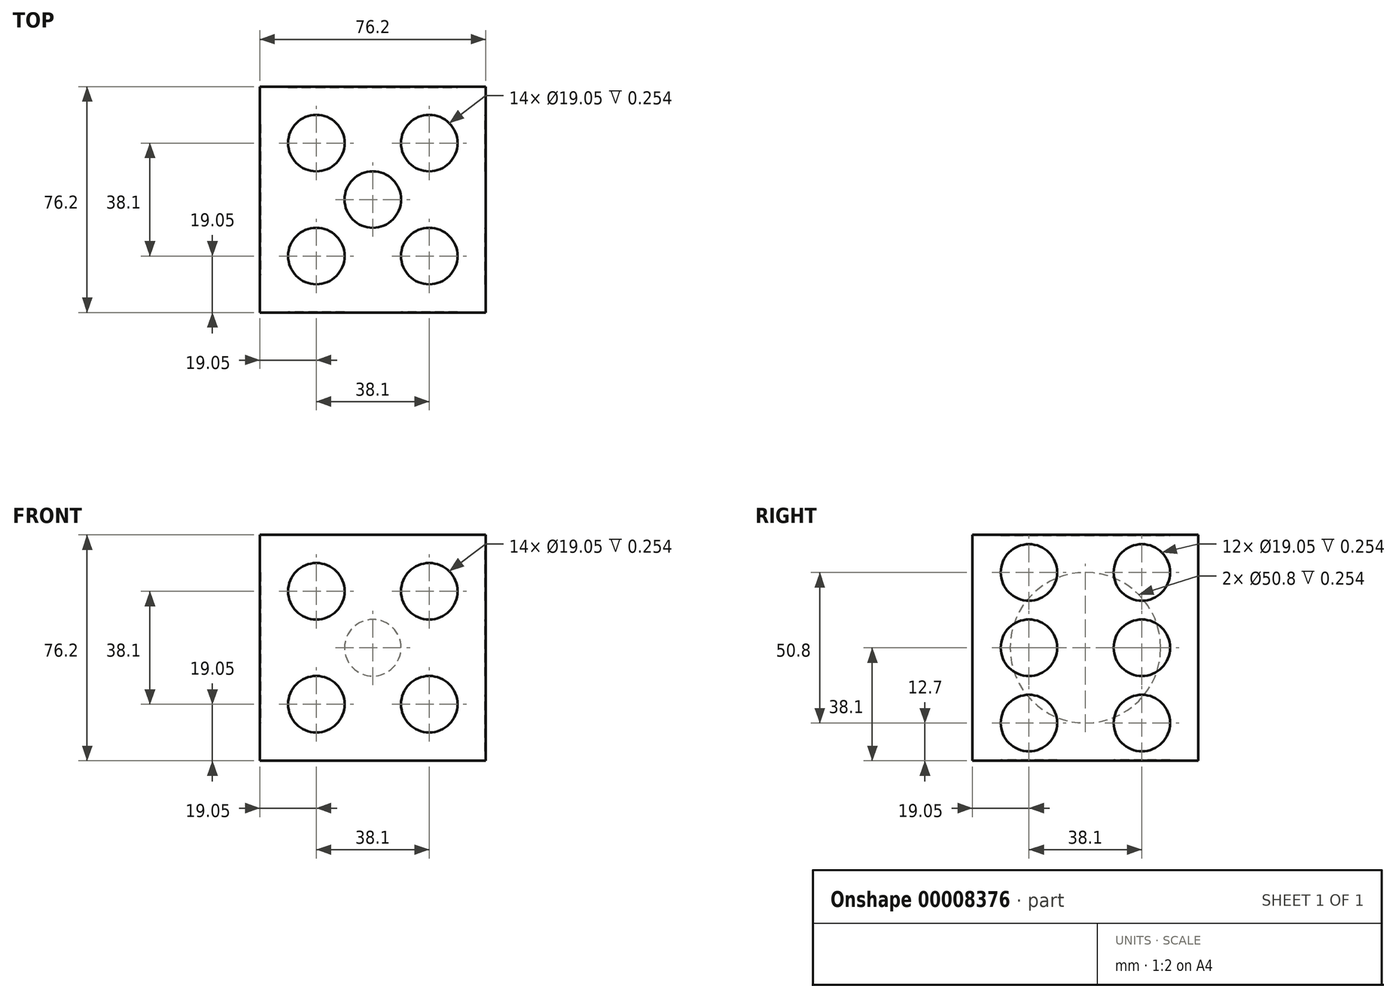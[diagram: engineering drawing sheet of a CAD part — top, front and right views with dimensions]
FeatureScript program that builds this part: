
annotation { "Feature Type Name" : "Feature", "Feature Type Description" : "" }
export const myFeature = defineFeature(function(context is Context, id is Id, definition is map)
    precondition{}
    {
        {
            var Q0;
            Q0=qCreatedBy(makeId("Top.planeOp"),FACE);
            var sketch = newSketch(context, id + "F0", { "sketchPlane" : qUnion([Q0])});
            skLineSegment(sketch, "E0.rect.bottom", {"start": v(38.1, -38.1) * mm, "end": v(-38.1, -38.1) * mm});
            skLineSegment(sketch, "E0.rect.top", {"start": v(38.1, 38.1) * mm, "end": v(-38.1, 38.1) * mm});
            skLineSegment(sketch, "E0.rect.left", {"start": v(38.1, -38.1) * mm, "end": v(38.1, 38.1) * mm});
            skLineSegment(sketch, "E0.rect.right", {"start": v(-38.1, -38.1) * mm, "end": v(-38.1, 38.1) * mm});
            skPoint(sketch, "E0.rect.middle", {"position": v(0, 0) * mm});
            skSolve(sketch);
        }
        {
            var Q0;
            Q0=makeQuery(id+"F0.imprint","IMPRINT",FACE,{"disambiguationData":[TD([[makeQuery(id+"F0.imprint","IMPRINT",EDGE,{"derivedFrom":sQuery(id+"F0.wireOp",EDGE,"E0.rect.bottom")}),-1.0]])]});
            extrude(context, id + "F1", {"entities" : qUnion([Q0]), "depth" : 38.1 * mm, "hasSecondDirection" : true, "secondDirectionOppositeDirection" : true, "secondDirectionDepth" : 38.1 * mm});
        }
        {
            var Q0;
            Q0=makeQuery(id+"F1.opExtrude","SWEPT_FACE",FACE,{"disambiguationData":[OSD([sQuery(id+"F0.wireOp",EDGE,"E0.rect.right")])]});
            var sketch = newSketch(context, id + "F2", { "sketchPlane" : qUnion([Q0])});
            skCircle(sketch, "E1", {"center": v(0, 0) * mm, "radius": 25.4 * mm});
            skSolve(sketch);
        }
        {
            var Q0;
            Q0=makeQuery(id+"F2.imprint","IMPRINT",FACE,{"disambiguationData":[TD([[makeQuery(id+"F2.imprint","IMPRINT",EDGE,{"derivedFrom":sQuery(id+"F2.wireOp",EDGE,"E1")}),1.0]])]});
            extrude(context, id + "F3", {"entities" : qUnion([Q0]), "operationType" : NewBodyOperationType.REMOVE, "oppositeDirection" : true, "depth" : 0.25 * mm});
        }
        {
            var Q0;
            Q0=makeQuery(id+"F1.opExtrude","SWEPT_FACE",FACE,{"disambiguationData":[OSD([sQuery(id+"F0.wireOp",EDGE,"E0.rect.left")])]});
            var sketch = newSketch(context, id + "F4", { "sketchPlane" : qUnion([Q0])});
            skCircle(sketch, "E2", {"center": v(-19.05, 25.4) * mm, "radius": 9.53 * mm});
            skCircle(sketch, "E3", {"center": v(-19.05, 0) * mm, "radius": 9.53 * mm});
            skCircle(sketch, "E4", {"center": v(-19.05, -25.4) * mm, "radius": 9.53 * mm});
            skCircle(sketch, "E5", {"center": v(19.05, -25.4) * mm, "radius": 9.53 * mm});
            skCircle(sketch, "E6", {"center": v(19.05, 0) * mm, "radius": 9.53 * mm});
            skCircle(sketch, "E7", {"center": v(19.05, 25.4) * mm, "radius": 9.53 * mm});
            skSolve(sketch);
        }
        {
            var Q0;
            Q0=makeQuery(id+"F4.imprint","IMPRINT",FACE,{"disambiguationData":[TD([[makeQuery(id+"F4.imprint","IMPRINT",EDGE,{"derivedFrom":sQuery(id+"F4.wireOp",EDGE,"E2")}),1.0]])]});
            var Q1;
            Q1=makeQuery(id+"F4.imprint","IMPRINT",FACE,{"disambiguationData":[TD([[makeQuery(id+"F4.imprint","IMPRINT",EDGE,{"derivedFrom":sQuery(id+"F4.wireOp",EDGE,"E7")}),1.0]])]});
            var Q2;
            Q2=makeQuery(id+"F4.imprint","IMPRINT",FACE,{"disambiguationData":[TD([[makeQuery(id+"F4.imprint","IMPRINT",EDGE,{"derivedFrom":sQuery(id+"F4.wireOp",EDGE,"E6")}),1.0]])]});
            var Q3;
            Q3=makeQuery(id+"F4.imprint","IMPRINT",FACE,{"disambiguationData":[TD([[makeQuery(id+"F4.imprint","IMPRINT",EDGE,{"derivedFrom":sQuery(id+"F4.wireOp",EDGE,"E5")}),1.0]])]});
            var Q4;
            Q4=makeQuery(id+"F4.imprint","IMPRINT",FACE,{"disambiguationData":[TD([[makeQuery(id+"F4.imprint","IMPRINT",EDGE,{"derivedFrom":sQuery(id+"F4.wireOp",EDGE,"E4")}),1.0]])]});
            var Q5;
            Q5=makeQuery(id+"F4.imprint","IMPRINT",FACE,{"disambiguationData":[TD([[makeQuery(id+"F4.imprint","IMPRINT",EDGE,{"derivedFrom":sQuery(id+"F4.wireOp",EDGE,"E3")}),1.0]])]});
            extrude(context, id + "F5", {"entities" : qUnion([Q0, Q1, Q2, Q3, Q4, Q5]), "operationType" : NewBodyOperationType.REMOVE, "oppositeDirection" : true, "depth" : 0.25 * mm});
        }
        {
            var Q0;
            Q0=makeQuery(id+"F1.opExtrude","SWEPT_FACE",FACE,{"disambiguationData":[OSD([sQuery(id+"F0.wireOp",EDGE,"E0.rect.top")])]});
            var sketch = newSketch(context, id + "F6", { "sketchPlane" : qUnion([Q0])});
            skCircle(sketch, "E8", {"center": v(19.05, 19.05) * mm, "radius": 9.53 * mm});
            skCircle(sketch, "E9", {"center": v(0, 0) * mm, "radius": 9.53 * mm});
            skCircle(sketch, "E10", {"center": v(-19.05, -19.05) * mm, "radius": 9.53 * mm});
            skSolve(sketch);
        }
        {
            var Q0;
            Q0=makeQuery(id+"F6.imprint","IMPRINT",FACE,{"disambiguationData":[TD([[makeQuery(id+"F6.imprint","IMPRINT",EDGE,{"derivedFrom":sQuery(id+"F6.wireOp",EDGE,"E10")}),1.0]])]});
            var Q1;
            Q1=makeQuery(id+"F6.imprint","IMPRINT",FACE,{"disambiguationData":[TD([[makeQuery(id+"F6.imprint","IMPRINT",EDGE,{"derivedFrom":sQuery(id+"F6.wireOp",EDGE,"E9")}),1.0]])]});
            var Q2;
            Q2=makeQuery(id+"F6.imprint","IMPRINT",FACE,{"disambiguationData":[TD([[makeQuery(id+"F6.imprint","IMPRINT",EDGE,{"derivedFrom":sQuery(id+"F6.wireOp",EDGE,"E8")}),1.0]])]});
            extrude(context, id + "F7", {"entities" : qUnion([Q0, Q1, Q2]), "operationType" : NewBodyOperationType.REMOVE, "oppositeDirection" : true, "depth" : 0.25 * mm});
        }
        {
            var Q0;
            Q0=makeQuery(id+"F1.opExtrude","SWEPT_FACE",FACE,{"disambiguationData":[OSD([sQuery(id+"F0.wireOp",EDGE,"E0.rect.bottom")])]});
            var sketch = newSketch(context, id + "F8", { "sketchPlane" : qUnion([Q0])});
            skCircle(sketch, "E11", {"center": v(-19.05, 19.05) * mm, "radius": 9.53 * mm});
            skCircle(sketch, "E12", {"center": v(19.05, 19.05) * mm, "radius": 9.53 * mm});
            skCircle(sketch, "E13", {"center": v(19.05, -19.05) * mm, "radius": 9.53 * mm});
            skCircle(sketch, "E14", {"center": v(-19.05, -19.05) * mm, "radius": 9.53 * mm});
            skSolve(sketch);
        }
        {
            var Q0;
            Q0=makeQuery(id+"F8.imprint","IMPRINT",FACE,{"disambiguationData":[TD([[makeQuery(id+"F8.imprint","IMPRINT",EDGE,{"derivedFrom":sQuery(id+"F8.wireOp",EDGE,"E11")}),1.0]])]});
            var Q1;
            Q1=makeQuery(id+"F8.imprint","IMPRINT",FACE,{"disambiguationData":[TD([[makeQuery(id+"F8.imprint","IMPRINT",EDGE,{"derivedFrom":sQuery(id+"F8.wireOp",EDGE,"E12")}),1.0]])]});
            var Q2;
            Q2=makeQuery(id+"F8.imprint","IMPRINT",FACE,{"disambiguationData":[TD([[makeQuery(id+"F8.imprint","IMPRINT",EDGE,{"derivedFrom":sQuery(id+"F8.wireOp",EDGE,"E13")}),1.0]])]});
            var Q3;
            Q3=makeQuery(id+"F8.imprint","IMPRINT",FACE,{"disambiguationData":[TD([[makeQuery(id+"F8.imprint","IMPRINT",EDGE,{"derivedFrom":sQuery(id+"F8.wireOp",EDGE,"E14")}),1.0]])]});
            extrude(context, id + "F9", {"entities" : qUnion([Q0, Q1, Q2, Q3]), "operationType" : NewBodyOperationType.REMOVE, "oppositeDirection" : true, "depth" : 0.25 * mm});
        }
        {
            var Q0;
            Q0=makeQuery(id+"F1.opExtrude","CAP_FACE",FACE,{"disambiguationData":[OSD([sQuery(id+"F0.wireOp",EDGE,"E0.rect.bottom"),sQuery(id+"F0.wireOp",EDGE,"E0.rect.top"),sQuery(id+"F0.wireOp",EDGE,"E0.rect.left"),sQuery(id+"F0.wireOp",EDGE,"E0.rect.right")])],"isStart":true});
            var sketch = newSketch(context, id + "F10", { "sketchPlane" : qUnion([Q0])});
            skCircle(sketch, "E15", {"center": v(-19.05, 19.05) * mm, "radius": 9.53 * mm});
            skCircle(sketch, "E16", {"center": v(19.05, -19.05) * mm, "radius": 9.53 * mm});
            skSolve(sketch);
        }
        {
            var Q0;
            Q0=makeQuery(id+"F10.imprint","IMPRINT",FACE,{"disambiguationData":[TD([[makeQuery(id+"F10.imprint","IMPRINT",EDGE,{"derivedFrom":sQuery(id+"F10.wireOp",EDGE,"E15")}),1.0]])]});
            var Q1;
            Q1=makeQuery(id+"F10.imprint","IMPRINT",FACE,{"disambiguationData":[TD([[makeQuery(id+"F10.imprint","IMPRINT",EDGE,{"derivedFrom":sQuery(id+"F10.wireOp",EDGE,"E16")}),1.0]])]});
            extrude(context, id + "F11", {"entities" : qUnion([Q0, Q1]), "operationType" : NewBodyOperationType.REMOVE, "oppositeDirection" : true, "depth" : 0.25 * mm});
        }
        {
            var Q0;
            Q0=makeQuery(id+"F1.opExtrude","CAP_FACE",FACE,{"disambiguationData":[OSD([sQuery(id+"F0.wireOp",EDGE,"E0.rect.bottom"),sQuery(id+"F0.wireOp",EDGE,"E0.rect.top"),sQuery(id+"F0.wireOp",EDGE,"E0.rect.left"),sQuery(id+"F0.wireOp",EDGE,"E0.rect.right")])],"isStart":false});
            var sketch = newSketch(context, id + "F12", { "sketchPlane" : qUnion([Q0])});
            skCircle(sketch, "E17", {"center": v(-19.05, 19.05) * mm, "radius": 9.53 * mm});
            skCircle(sketch, "E18", {"center": v(19.05, 19.05) * mm, "radius": 9.53 * mm});
            skCircle(sketch, "E19", {"center": v(0, 0) * mm, "radius": 9.53 * mm});
            skCircle(sketch, "E20", {"center": v(19.05, -19.05) * mm, "radius": 9.53 * mm});
            skCircle(sketch, "E21", {"center": v(-19.05, -19.05) * mm, "radius": 9.53 * mm});
            skSolve(sketch);
        }
        {
            var Q0;
            Q0=makeQuery(id+"F12.imprint","IMPRINT",FACE,{"disambiguationData":[TD([[makeQuery(id+"F12.imprint","IMPRINT",EDGE,{"derivedFrom":sQuery(id+"F12.wireOp",EDGE,"E17")}),1.0]])]});
            var Q1;
            Q1=makeQuery(id+"F12.imprint","IMPRINT",FACE,{"disambiguationData":[TD([[makeQuery(id+"F12.imprint","IMPRINT",EDGE,{"derivedFrom":sQuery(id+"F12.wireOp",EDGE,"E19")}),1.0]])]});
            var Q2;
            Q2=makeQuery(id+"F12.imprint","IMPRINT",FACE,{"disambiguationData":[TD([[makeQuery(id+"F12.imprint","IMPRINT",EDGE,{"derivedFrom":sQuery(id+"F12.wireOp",EDGE,"E18")}),1.0]])]});
            var Q3;
            Q3=makeQuery(id+"F12.imprint","IMPRINT",FACE,{"disambiguationData":[TD([[makeQuery(id+"F12.imprint","IMPRINT",EDGE,{"derivedFrom":sQuery(id+"F12.wireOp",EDGE,"E20")}),1.0]])]});
            var Q4;
            Q4=makeQuery(id+"F12.imprint","IMPRINT",FACE,{"disambiguationData":[TD([[makeQuery(id+"F12.imprint","IMPRINT",EDGE,{"derivedFrom":sQuery(id+"F12.wireOp",EDGE,"E21")}),1.0]])]});
            extrude(context, id + "F13", {"entities" : qUnion([Q0, Q1, Q2, Q3, Q4]), "operationType" : NewBodyOperationType.REMOVE, "oppositeDirection" : true, "depth" : 0.25 * mm});
        }
    });
